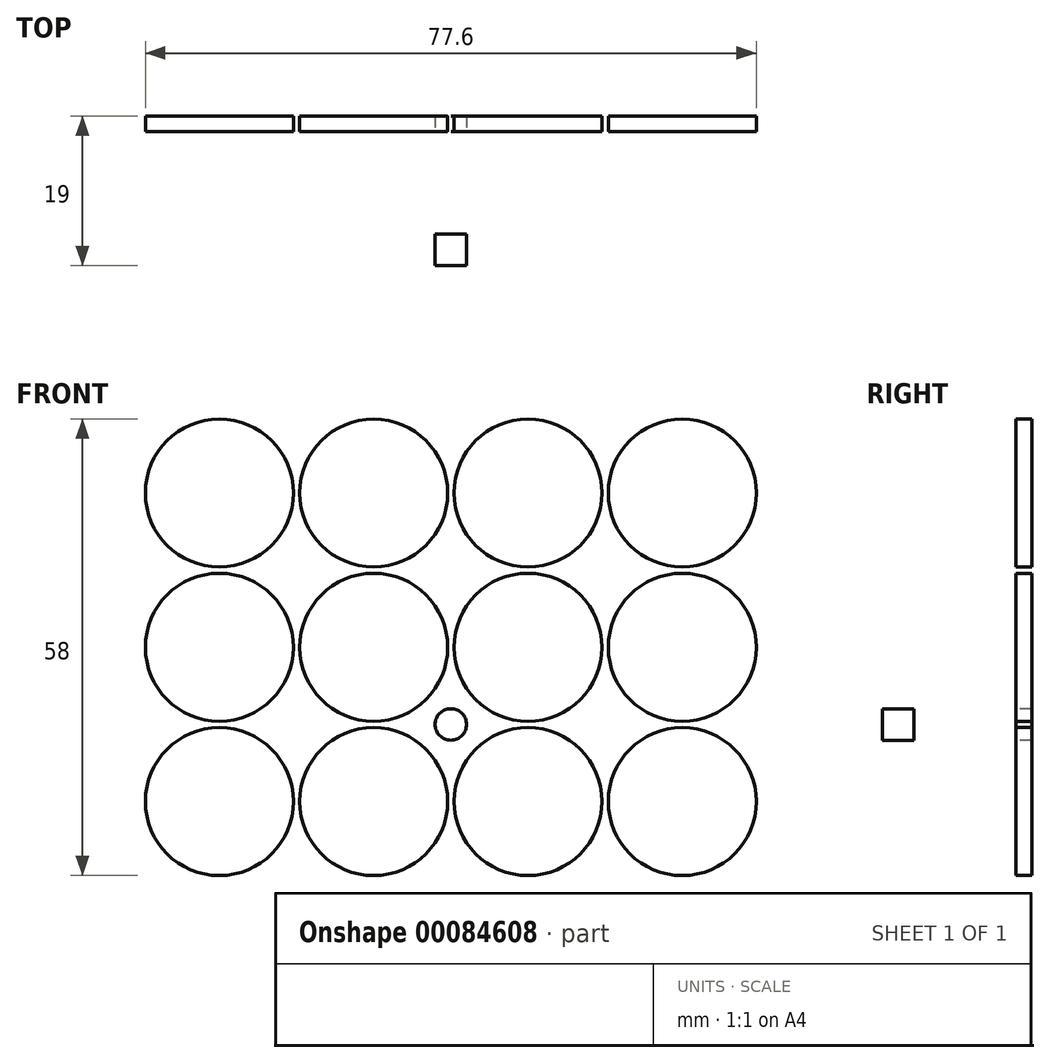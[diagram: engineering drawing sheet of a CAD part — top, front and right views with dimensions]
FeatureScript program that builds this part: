
annotation { "Feature Type Name" : "Feature", "Feature Type Description" : "" }
export const myFeature = defineFeature(function(context is Context, id is Id, definition is map)
    precondition{}
    {
        {
            var Q0;
            Q0=qCreatedBy(makeId("Front.planeOp"),FACE);
            var sketch = newSketch(context, id + "F0", { "sketchPlane" : qUnion([Q0]) });
            skCircle(sketch, "E0", {"center": v(0, 0) * mm, "radius": 9.4 * mm});
            skCircle(sketch, "E1.1.0.0", {"center": v(19.6, 0) * mm, "radius": 9.4 * mm});
            skCircle(sketch, "E1.2.0.0", {"center": v(39.2, 0) * mm, "radius": 9.4 * mm});
            skCircle(sketch, "E1.3.0.0", {"center": v(58.8, 0) * mm, "radius": 9.4 * mm});
            skLineSegment(sketch, "E1.direction1", {"start": v(0, 0) * mm, "end": v(19.6, 0) * mm, "construction": true});
            skArc(sketch, "E2", {"start": v(58.8, 9.4) * mm, "mid": v(63.5, 8.14) * mm, "end": v(66.94, 4.7) * mm});
            skArc(sketch, "E3", {"start": v(-8.14, -4.7) * mm, "mid": v(-8.14, 4.7) * mm, "end": v(0, 9.4) * mm});
            skArc(sketch, "E4.0", {"start": v(0, 11.4) * mm, "mid": v(-9.87, 5.7) * mm, "end": v(-9.88, -5.7) * mm});
            skCircle(sketch, "E5.0.1.0", {"center": v(19.6, -19.6) * mm, "radius": 9.4 * mm});
            skCircle(sketch, "E5.0.1.1", {"center": v(39.2, -19.6) * mm, "radius": 9.4 * mm});
            skCircle(sketch, "E5.0.1.2", {"center": v(58.8, -19.6) * mm, "radius": 9.4 * mm});
            skCircle(sketch, "E5.0.1.3", {"center": v(0, -19.6) * mm, "radius": 9.4 * mm});
            skCircle(sketch, "E5.0.2.0", {"center": v(19.6, -39.2) * mm, "radius": 9.4 * mm});
            skCircle(sketch, "E5.0.2.1", {"center": v(39.2, -39.2) * mm, "radius": 9.4 * mm});
            skCircle(sketch, "E5.0.2.2", {"center": v(58.8, -39.2) * mm, "radius": 9.4 * mm});
            skCircle(sketch, "E5.0.2.3", {"center": v(0, -39.2) * mm, "radius": 9.4 * mm});
            skLineSegment(sketch, "E5.direction1", {"start": v(19.6, 0) * mm, "end": v(44.6, 0) * mm, "construction": true});
            skLineSegment(sketch, "E5.direction2", {"start": v(19.6, 0) * mm, "end": v(19.6, -19.6) * mm, "construction": true});
            skArc(sketch, "E6.0", {"start": v(9.8, -45.02) * mm, "mid": v(19.6, -50.6) * mm, "end": v(29.4, -45.02) * mm});
            skArc(sketch, "E7.0", {"start": v(29.4, -45.02) * mm, "mid": v(39.2, -50.6) * mm, "end": v(49, -45.02) * mm});
            skArc(sketch, "E8.0", {"start": v(49, -45.02) * mm, "mid": v(66.86, -47.26) * mm, "end": v(64.62, -29.4) * mm});
            skArc(sketch, "E9.trimOffspring", {"start": v(64.62, -29.4) * mm, "mid": v(70.2, -19.6) * mm, "end": v(64.62, -9.8) * mm});
            skArc(sketch, "E10.trimOffspring", {"start": v(64.62, -9.8) * mm, "mid": v(66.86, 8.06) * mm, "end": v(49, 5.82) * mm});
            skArc(sketch, "E11.trimOffspring", {"start": v(-5.82, -29.4) * mm, "mid": v(-8.06, -47.26) * mm, "end": v(9.8, -45.02) * mm});
            skArc(sketch, "E12.trimOffspring", {"start": v(-5.82, -9.8) * mm, "mid": v(-11.4, -19.6) * mm, "end": v(-5.82, -29.4) * mm});
            skArc(sketch, "E13.trimOffspring", {"start": v(9.8, 5.82) * mm, "mid": v(-8.06, 8.06) * mm, "end": v(-5.82, -9.8) * mm});
            skArc(sketch, "E14.trimOffspring", {"start": v(29.4, 5.82) * mm, "mid": v(19.6, 11.4) * mm, "end": v(9.8, 5.82) * mm});
            skArc(sketch, "E15.trimOffspring", {"start": v(49, 5.82) * mm, "mid": v(39.2, 11.4) * mm, "end": v(29.4, 5.82) * mm});
            skLineSegment(sketch, "E16", {"start": v(-11.4, -19.6) * mm, "end": v(70.2, -19.6) * mm, "construction": true});
            skLineSegment(sketch, "E17", {"start": v(0, 11.4) * mm, "end": v(-11.4, 11.4) * mm, "construction": true});
            skLineSegment(sketch, "E18", {"start": v(-11.4, 0) * mm, "end": v(-11.4, 11.4) * mm, "construction": true});
            skLineSegment(sketch, "E19", {"start": v(58.8, -50.6) * mm, "end": v(70.2, -50.6) * mm, "construction": true});
            skLineSegment(sketch, "E20", {"start": v(70.2, -50.6) * mm, "end": v(70.2, -39.2) * mm, "construction": true});
            skLineSegment(sketch, "E21.bottom", {"start": v(-11.4, 11.4) * mm, "end": v(70.2, 11.4) * mm, "construction": true});
            skLineSegment(sketch, "E21.top", {"start": v(-11.4, -50.6) * mm, "end": v(70.2, -50.6) * mm, "construction": true});
            skLineSegment(sketch, "E21.left", {"start": v(-11.4, 11.4) * mm, "end": v(-11.4, -50.6) * mm, "construction": true});
            skLineSegment(sketch, "E21.right", {"start": v(70.2, 11.4) * mm, "end": v(70.2, -50.6) * mm, "construction": true});
            skSolve(sketch);
        }
        {
            var Q0;
            Q0=qSketchRegion(id+"F0",true);
            extrude(context, id + "F1", {"entities" : qUnion([Q0]), "depth" : 4 * mm});
        }
        {
            var Q0;
            Q0=makeQuery(id+"F1.opExtrude","CAP_FACE",FACE,{"disambiguationData":[OSD([sQuery(id+"F0.wireOp",EDGE,"E0"),sQuery(id+"F0.wireOp",EDGE,"E1.1.0.0"),sQuery(id+"F0.wireOp",EDGE,"E1.2.0.0"),sQuery(id+"F0.wireOp",EDGE,"E1.3.0.0"),sQuery(id+"F0.wireOp",EDGE,"E5.0.1.0"),sQuery(id+"F0.wireOp",EDGE,"E5.0.1.1"),sQuery(id+"F0.wireOp",EDGE,"E5.0.1.2"),sQuery(id+"F0.wireOp",EDGE,"E5.0.1.3"),sQuery(id+"F0.wireOp",EDGE,"E5.0.2.0"),sQuery(id+"F0.wireOp",EDGE,"E5.0.2.1"),sQuery(id+"F0.wireOp",EDGE,"E5.0.2.2"),sQuery(id+"F0.wireOp",EDGE,"E5.0.2.3"),sQuery(id+"F0.wireOp",EDGE,"E6.0"),sQuery(id+"F0.wireOp",EDGE,"E7.0"),sQuery(id+"F0.wireOp",EDGE,"E8.0"),sQuery(id+"F0.wireOp",EDGE,"E9.trimOffspring"),sQuery(id+"F0.wireOp",EDGE,"E10.trimOffspring"),sQuery(id+"F0.wireOp",EDGE,"E11.trimOffspring"),sQuery(id+"F0.wireOp",EDGE,"E12.trimOffspring"),sQuery(id+"F0.wireOp",EDGE,"E13.trimOffspring"),sQuery(id+"F0.wireOp",EDGE,"E14.trimOffspring"),sQuery(id+"F0.wireOp",EDGE,"E15.trimOffspring")])],"isStart":true});
            var sketch = newSketch(context, id + "F2", { "sketchPlane" : qUnion([Q0]) });
            skArc(sketch, "E22.0", {"start": v(5.82, -29.4) * mm, "mid": v(8.06, -47.26) * mm, "end": v(-9.8, -45.02) * mm});
            skArc(sketch, "E22.1", {"start": v(-9.8, -45.02) * mm, "mid": v(-19.6, -50.6) * mm, "end": v(-29.4, -45.02) * mm});
            skArc(sketch, "E22.2", {"start": v(-29.4, -45.02) * mm, "mid": v(-39.2, -50.6) * mm, "end": v(-49, -45.02) * mm});
            skArc(sketch, "E22.3", {"start": v(-49, -45.02) * mm, "mid": v(-66.86, -47.26) * mm, "end": v(-64.62, -29.4) * mm});
            skArc(sketch, "E22.4", {"start": v(5.82, -9.8) * mm, "mid": v(11.4, -19.6) * mm, "end": v(5.82, -29.4) * mm});
            skArc(sketch, "E22.5", {"start": v(-9.8, 5.82) * mm, "mid": v(8.06, 8.06) * mm, "end": v(5.82, -9.8) * mm});
            skArc(sketch, "E22.6", {"start": v(-29.4, 5.82) * mm, "mid": v(-19.6, 11.4) * mm, "end": v(-9.8, 5.82) * mm});
            skArc(sketch, "E22.7", {"start": v(-49, 5.82) * mm, "mid": v(-39.2, 11.4) * mm, "end": v(-29.4, 5.82) * mm});
            skArc(sketch, "E22.8", {"start": v(-64.62, -9.8) * mm, "mid": v(-66.86, 8.06) * mm, "end": v(-49, 5.82) * mm});
            skArc(sketch, "E22.9", {"start": v(-64.62, -29.4) * mm, "mid": v(-70.2, -19.6) * mm, "end": v(-64.62, -9.8) * mm});
            skArc(sketch, "E22.10", {"start": v(-7.32, -45.1) * mm, "mid": v(6.65, -45.85) * mm, "end": v(5.9, -31.88) * mm});
            skArc(sketch, "E22.11", {"start": v(-26.92, -45.1) * mm, "mid": v(-19.6, -48.6) * mm, "end": v(-12.28, -45.1) * mm});
            skArc(sketch, "E22.12", {"start": v(-46.52, -45.1) * mm, "mid": v(-39.2, -48.6) * mm, "end": v(-31.88, -45.1) * mm});
            skArc(sketch, "E22.13", {"start": v(-64.7, -31.88) * mm, "mid": v(-65.45, -45.85) * mm, "end": v(-51.48, -45.1) * mm});
            skArc(sketch, "E22.14", {"start": v(-64.7, -12.28) * mm, "mid": v(-68.2, -19.6) * mm, "end": v(-64.7, -26.92) * mm});
            skArc(sketch, "E22.15", {"start": v(5.9, -26.92) * mm, "mid": v(9.4, -19.6) * mm, "end": v(5.9, -12.28) * mm});
            skArc(sketch, "E22.16", {"start": v(5.9, -7.32) * mm, "mid": v(6.65, 6.65) * mm, "end": v(-7.32, 5.9) * mm});
            skArc(sketch, "E22.17", {"start": v(-12.28, 5.9) * mm, "mid": v(-19.6, 9.4) * mm, "end": v(-26.92, 5.9) * mm});
            skArc(sketch, "E22.18", {"start": v(-31.88, 5.9) * mm, "mid": v(-39.2, 9.4) * mm, "end": v(-46.52, 5.9) * mm});
            skArc(sketch, "E22.19", {"start": v(-51.48, 5.9) * mm, "mid": v(-65.45, 6.65) * mm, "end": v(-64.7, -7.32) * mm});
            skLineSegment(sketch, "E23", {"start": v(-9.8, -45.02) * mm, "end": v(-9.8, -42.02) * mm, "construction": true});
            skLineSegment(sketch, "E24", {"start": v(-9.41, -42.5) * mm, "end": v(-7.32, -45.1) * mm});
            skLineSegment(sketch, "E25.MirrorCS", {"start": v(-10.19, -42.5) * mm, "end": v(-12.28, -45.1) * mm});
            skPoint(sketch, "E26.visualSharp", {"position": v(-9.8, -42.02) * mm});
            skArc(sketch, "E26.filletArc", {"start": v(-9.41, -42.5) * mm, "mid": v(-9.8, -42.32) * mm, "end": v(-10.19, -42.5) * mm});
            skLineSegment(sketch, "E27.1.0.0", {"start": v(-29.01, -42.5) * mm, "end": v(-26.92, -45.1) * mm});
            skArc(sketch, "E27.1.0.1", {"start": v(-29.01, -42.5) * mm, "mid": v(-29.4, -42.32) * mm, "end": v(-29.79, -42.5) * mm});
            skLineSegment(sketch, "E27.1.0.2", {"start": v(-29.79, -42.5) * mm, "end": v(-31.88, -45.1) * mm});
            skLineSegment(sketch, "E27.2.0.0", {"start": v(-48.61, -42.5) * mm, "end": v(-46.52, -45.1) * mm});
            skArc(sketch, "E27.2.0.1", {"start": v(-48.61, -42.5) * mm, "mid": v(-49, -42.32) * mm, "end": v(-49.39, -42.5) * mm});
            skLineSegment(sketch, "E27.2.0.2", {"start": v(-49.39, -42.5) * mm, "end": v(-51.48, -45.1) * mm});
            skLineSegment(sketch, "E27.direction1", {"start": v(-7.32, -45.1) * mm, "end": v(-26.92, -45.1) * mm, "construction": true});
            skLineSegment(sketch, "E28", {"start": v(0, -19.6) * mm, "end": v(-58.8, -19.6) * mm, "construction": true});
            skLineSegment(sketch, "E29.MirrorCS", {"start": v(-9.41, 3.3) * mm, "end": v(-7.32, 5.9) * mm});
            skArc(sketch, "E30.MirrorCS", {"start": v(-9.41, 3.3) * mm, "mid": v(-9.8, 3.12) * mm, "end": v(-10.19, 3.3) * mm});
            skLineSegment(sketch, "E31.MirrorCS", {"start": v(-10.19, 3.3) * mm, "end": v(-12.28, 5.9) * mm});
            skLineSegment(sketch, "E32.MirrorCS", {"start": v(-29.01, 3.3) * mm, "end": v(-26.92, 5.9) * mm});
            skArc(sketch, "E33.MirrorCS", {"start": v(-29.01, 3.3) * mm, "mid": v(-29.4, 3.12) * mm, "end": v(-29.79, 3.3) * mm});
            skLineSegment(sketch, "E34.MirrorCS", {"start": v(-29.79, 3.3) * mm, "end": v(-31.88, 5.9) * mm});
            skLineSegment(sketch, "E35.MirrorCS", {"start": v(-48.61, 3.3) * mm, "end": v(-46.52, 5.9) * mm});
            skArc(sketch, "E36.MirrorCS", {"start": v(-48.61, 3.3) * mm, "mid": v(-49, 3.12) * mm, "end": v(-49.39, 3.3) * mm});
            skLineSegment(sketch, "E37.MirrorCS", {"start": v(-49.39, 3.3) * mm, "end": v(-51.48, 5.9) * mm});
            skLineSegment(sketch, "E38", {"start": v(5.82, -29.4) * mm, "end": v(2.82, -29.4) * mm, "construction": true});
            skLineSegment(sketch, "E39", {"start": v(3.3, -29.79) * mm, "end": v(5.9, -31.88) * mm});
            skLineSegment(sketch, "E40.MirrorCS", {"start": v(3.3, -29.01) * mm, "end": v(5.9, -26.92) * mm});
            skPoint(sketch, "E41.visualSharp", {"position": v(2.82, -29.4) * mm});
            skArc(sketch, "E41.filletArc", {"start": v(3.3, -29.01) * mm, "mid": v(3.12, -29.4) * mm, "end": v(3.3, -29.79) * mm});
            skLineSegment(sketch, "E42.MirrorCS", {"start": v(3.3, -10.19) * mm, "end": v(5.9, -12.28) * mm});
            skLineSegment(sketch, "E43.MirrorCS", {"start": v(3.3, -9.41) * mm, "end": v(5.9, -7.32) * mm});
            skArc(sketch, "E44.MirrorCS", {"start": v(3.3, -10.19) * mm, "mid": v(3.12, -9.8) * mm, "end": v(3.3, -9.41) * mm});
            skLineSegment(sketch, "E45", {"start": v(-29.4, -45.02) * mm, "end": v(-29.4, 5.82) * mm, "construction": true});
            skLineSegment(sketch, "E46.MirrorCS", {"start": v(-62.1, -29.79) * mm, "end": v(-64.7, -31.88) * mm});
            skLineSegment(sketch, "E47.MirrorCS", {"start": v(-62.1, -29.01) * mm, "end": v(-64.7, -26.92) * mm});
            skArc(sketch, "E48.MirrorCS", {"start": v(-62.1, -29.01) * mm, "mid": v(-61.92, -29.4) * mm, "end": v(-62.1, -29.79) * mm});
            skLineSegment(sketch, "E49.MirrorCS", {"start": v(-62.1, -10.19) * mm, "end": v(-64.7, -12.28) * mm});
            skLineSegment(sketch, "E50.MirrorCS", {"start": v(-62.1, -9.41) * mm, "end": v(-64.7, -7.32) * mm});
            skArc(sketch, "E51.MirrorCS", {"start": v(-62.1, -10.19) * mm, "mid": v(-61.92, -9.8) * mm, "end": v(-62.1, -9.41) * mm});
            skSolve(sketch);
        }
        {
            var Q0;
            Q0=makeQuery(id+"F2.imprint","IMPRINT",FACE,{"disambiguationData":[TD([[makeQuery(id+"F2.imprint","IMPRINT",EDGE,{"derivedFrom":sQuery(id+"F2.wireOp",EDGE,"E22.0")}),-1.0]])]});
            extrude(context, id + "F3", {"entities" : qUnion([Q0]), "depth" : 15 * mm});
        }
        {
            var Q0;
            Q0=makeQuery(id+"F3.opExtrude","CAP_FACE",FACE,{"disambiguationData":[OSD([sQuery(id+"F2.wireOp",EDGE,"E22.0"),sQuery(id+"F2.wireOp",EDGE,"E22.1"),sQuery(id+"F2.wireOp",EDGE,"E22.2"),sQuery(id+"F2.wireOp",EDGE,"E22.3"),sQuery(id+"F2.wireOp",EDGE,"E22.4"),sQuery(id+"F2.wireOp",EDGE,"E22.5"),sQuery(id+"F2.wireOp",EDGE,"E22.6"),sQuery(id+"F2.wireOp",EDGE,"E22.7"),sQuery(id+"F2.wireOp",EDGE,"E22.8"),sQuery(id+"F2.wireOp",EDGE,"E22.9"),sQuery(id+"F2.wireOp",EDGE,"E22.10"),sQuery(id+"F2.wireOp",EDGE,"E22.11"),sQuery(id+"F2.wireOp",EDGE,"E22.12"),sQuery(id+"F2.wireOp",EDGE,"E22.13"),sQuery(id+"F2.wireOp",EDGE,"E22.14"),sQuery(id+"F2.wireOp",EDGE,"E22.15"),sQuery(id+"F2.wireOp",EDGE,"E22.16"),sQuery(id+"F2.wireOp",EDGE,"E22.17"),sQuery(id+"F2.wireOp",EDGE,"E22.18"),sQuery(id+"F2.wireOp",EDGE,"E22.19"),sQuery(id+"F2.wireOp",EDGE,"E24"),sQuery(id+"F2.wireOp",EDGE,"E25.MirrorCS"),sQuery(id+"F2.wireOp",EDGE,"E26.filletArc"),sQuery(id+"F2.wireOp",EDGE,"E27.1.0.0"),sQuery(id+"F2.wireOp",EDGE,"E27.1.0.1"),sQuery(id+"F2.wireOp",EDGE,"E27.1.0.2"),sQuery(id+"F2.wireOp",EDGE,"E27.2.0.0"),sQuery(id+"F2.wireOp",EDGE,"E27.2.0.1"),sQuery(id+"F2.wireOp",EDGE,"E27.2.0.2"),sQuery(id+"F2.wireOp",EDGE,"E29.MirrorCS"),sQuery(id+"F2.wireOp",EDGE,"E30.MirrorCS"),sQuery(id+"F2.wireOp",EDGE,"E31.MirrorCS"),sQuery(id+"F2.wireOp",EDGE,"E32.MirrorCS"),sQuery(id+"F2.wireOp",EDGE,"E33.MirrorCS"),sQuery(id+"F2.wireOp",EDGE,"E34.MirrorCS"),sQuery(id+"F2.wireOp",EDGE,"E35.MirrorCS"),sQuery(id+"F2.wireOp",EDGE,"E36.MirrorCS"),sQuery(id+"F2.wireOp",EDGE,"E37.MirrorCS"),sQuery(id+"F2.wireOp",EDGE,"E39"),sQuery(id+"F2.wireOp",EDGE,"E40.MirrorCS"),sQuery(id+"F2.wireOp",EDGE,"E41.filletArc"),sQuery(id+"F2.wireOp",EDGE,"E42.MirrorCS"),sQuery(id+"F2.wireOp",EDGE,"E43.MirrorCS"),sQuery(id+"F2.wireOp",EDGE,"E44.MirrorCS"),sQuery(id+"F2.wireOp",EDGE,"E46.MirrorCS"),sQuery(id+"F2.wireOp",EDGE,"E47.MirrorCS"),sQuery(id+"F2.wireOp",EDGE,"E48.MirrorCS"),sQuery(id+"F2.wireOp",EDGE,"E49.MirrorCS"),sQuery(id+"F2.wireOp",EDGE,"E50.MirrorCS"),sQuery(id+"F2.wireOp",EDGE,"E51.MirrorCS")])],"isStart":false});
            var sketch = newSketch(context, id + "F4", { "sketchPlane" : qUnion([Q0]) });
            skArc(sketch, "E52.0", {"start": v(-9.8, -45.02) * mm, "mid": v(-19.6, -50.6) * mm, "end": v(-29.4, -45.02) * mm});
            skArc(sketch, "E52.1", {"start": v(5.82, -29.4) * mm, "mid": v(8.06, -47.26) * mm, "end": v(-9.8, -45.02) * mm});
            skArc(sketch, "E52.2", {"start": v(5.82, -9.8) * mm, "mid": v(11.4, -19.6) * mm, "end": v(5.82, -29.4) * mm});
            skArc(sketch, "E52.3", {"start": v(-9.8, 5.82) * mm, "mid": v(8.06, 8.06) * mm, "end": v(5.82, -9.8) * mm});
            skArc(sketch, "E52.4", {"start": v(-29.4, 5.82) * mm, "mid": v(-19.6, 11.4) * mm, "end": v(-9.8, 5.82) * mm});
            skArc(sketch, "E52.5", {"start": v(-49, 5.82) * mm, "mid": v(-39.2, 11.4) * mm, "end": v(-29.4, 5.82) * mm});
            skArc(sketch, "E52.6", {"start": v(-64.62, -9.8) * mm, "mid": v(-66.86, 8.06) * mm, "end": v(-49, 5.82) * mm});
            skArc(sketch, "E52.7", {"start": v(-64.62, -29.4) * mm, "mid": v(-70.2, -19.6) * mm, "end": v(-64.62, -9.8) * mm});
            skArc(sketch, "E52.8", {"start": v(-49, -45.02) * mm, "mid": v(-66.86, -47.26) * mm, "end": v(-64.62, -29.4) * mm});
            skArc(sketch, "E52.9", {"start": v(-29.4, -45.02) * mm, "mid": v(-39.2, -50.6) * mm, "end": v(-49, -45.02) * mm});
            skSolve(sketch);
        }
        {
            var Q0;
            Q0=makeQuery(id+"F4.imprint","IMPRINT",FACE,{"disambiguationData":[TD([[makeQuery(id+"F4.imprint","IMPRINT",EDGE,{"derivedFrom":makeQuery(id+"F3.opExtrude","CAP_EDGE",EDGE,{"disambiguationData":[OSD([sQuery(id+"F2.wireOp",EDGE,"E22.10")])],"isStart":false})}),-1.0]])]});
            extrude(context, id + "F5", {"entities" : qUnion([Q0]), "operationType" : NewBodyOperationType.ADD, "oppositeDirection" : true, "depth" : 2 * mm});
        }
        {
            var Q0;
            Q0=makeQuery(id+"F1.opExtrude","CAP_FACE",FACE,{"disambiguationData":[OSD([sQuery(id+"F0.wireOp",EDGE,"E0"),sQuery(id+"F0.wireOp",EDGE,"E1.1.0.0"),sQuery(id+"F0.wireOp",EDGE,"E1.2.0.0"),sQuery(id+"F0.wireOp",EDGE,"E1.3.0.0"),sQuery(id+"F0.wireOp",EDGE,"E5.0.1.0"),sQuery(id+"F0.wireOp",EDGE,"E5.0.1.1"),sQuery(id+"F0.wireOp",EDGE,"E5.0.1.2"),sQuery(id+"F0.wireOp",EDGE,"E5.0.1.3"),sQuery(id+"F0.wireOp",EDGE,"E5.0.2.0"),sQuery(id+"F0.wireOp",EDGE,"E5.0.2.1"),sQuery(id+"F0.wireOp",EDGE,"E5.0.2.2"),sQuery(id+"F0.wireOp",EDGE,"E5.0.2.3"),sQuery(id+"F0.wireOp",EDGE,"E6.0"),sQuery(id+"F0.wireOp",EDGE,"E7.0"),sQuery(id+"F0.wireOp",EDGE,"E8.0"),sQuery(id+"F0.wireOp",EDGE,"E9.trimOffspring"),sQuery(id+"F0.wireOp",EDGE,"E10.trimOffspring"),sQuery(id+"F0.wireOp",EDGE,"E11.trimOffspring"),sQuery(id+"F0.wireOp",EDGE,"E12.trimOffspring"),sQuery(id+"F0.wireOp",EDGE,"E13.trimOffspring"),sQuery(id+"F0.wireOp",EDGE,"E14.trimOffspring"),sQuery(id+"F0.wireOp",EDGE,"E15.trimOffspring")])],"isStart":false});
            var sketch = newSketch(context, id + "F6", { "sketchPlane" : qUnion([Q0]) });
            skCircle(sketch, "E53.0", {"center": v(19.6, 0) * mm, "radius": 9.4 * mm, "construction": true});
            skCircle(sketch, "E53.1", {"center": v(19.6, -19.6) * mm, "radius": 9.4 * mm, "construction": true});
            skCircle(sketch, "E53.2", {"center": v(39.2, -19.6) * mm, "radius": 9.4 * mm, "construction": true});
            skCircle(sketch, "E53.3", {"center": v(39.2, 0) * mm, "radius": 9.4 * mm, "construction": true});
            skLineSegment(sketch, "E54", {"start": v(19.6, 0) * mm, "end": v(39.2, -19.6) * mm, "construction": true});
            skCircle(sketch, "E55", {"center": v(29.4, -9.8) * mm, "radius": 2 * mm});
            skLineSegment(sketch, "E56", {"start": v(19.6, -19.6) * mm, "end": v(39.2, -19.6) * mm, "construction": true});
            skCircle(sketch, "E57.MirrorC", {"center": v(29.4, -29.4) * mm, "radius": 2 * mm});
            skSolve(sketch);
        }
        {
            var Q0;
            Q0=makeQuery(id+"F6.imprint","IMPRINT",FACE,{"disambiguationData":[TD([[makeQuery(id+"F6.imprint","IMPRINT",EDGE,{"derivedFrom":sQuery(id+"F6.wireOp",EDGE,"E55")}),1.0]])]});
            var Q1;
            Q1=makeQuery(id+"F6.imprint","IMPRINT",FACE,{"disambiguationData":[TD([[makeQuery(id+"F6.imprint","IMPRINT",EDGE,{"derivedFrom":sQuery(id+"F6.wireOp",EDGE,"E57.MirrorC")}),-1.0]])]});
            extrude(context, id + "F7", {"entities" : qUnion([Q0, Q1]), "operationType" : NewBodyOperationType.REMOVE, "endBound" : BoundingType.THROUGH_ALL, "oppositeDirection" : true, "depth" : 25 * mm});
        }
    });
